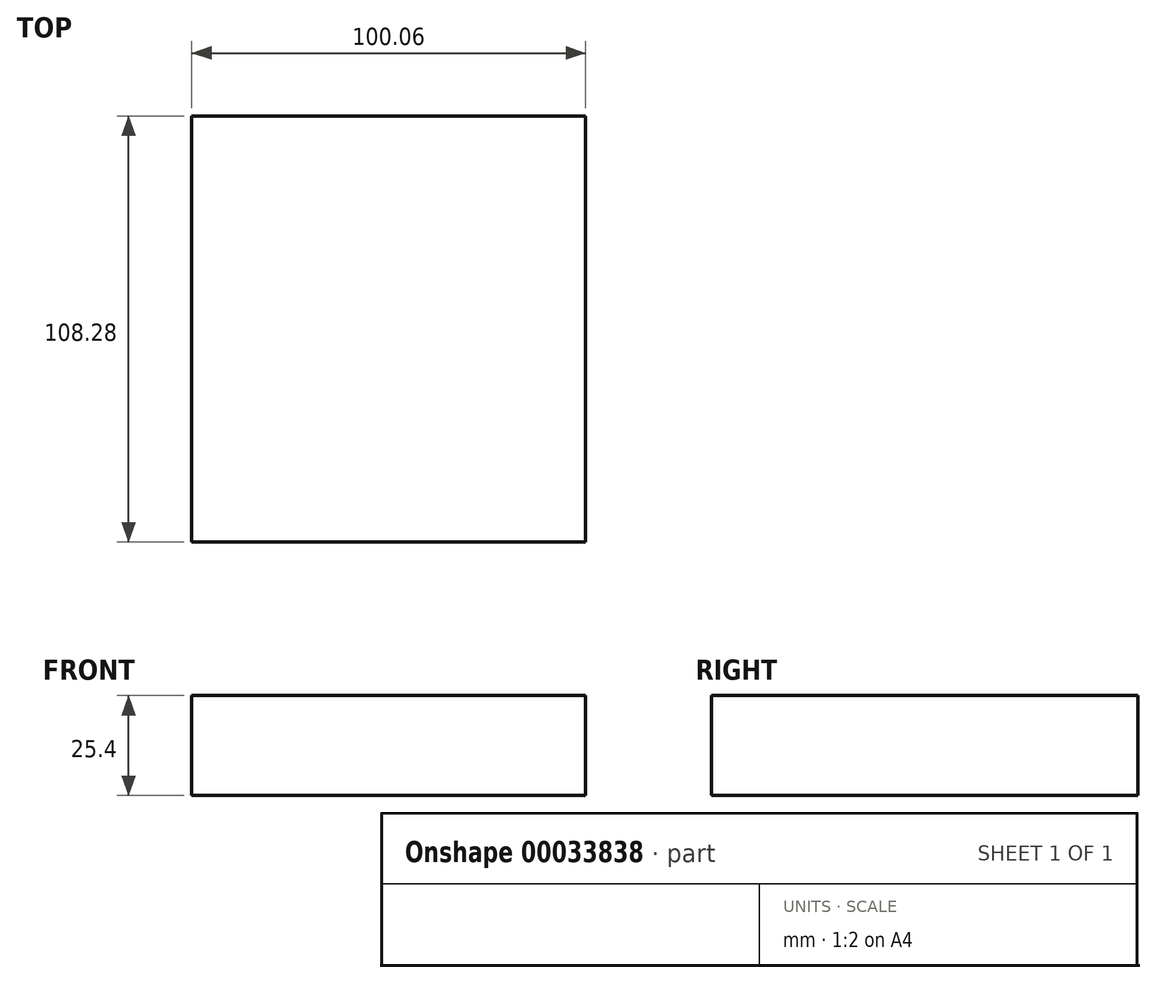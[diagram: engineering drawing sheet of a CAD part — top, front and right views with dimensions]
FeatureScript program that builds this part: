
annotation { "Feature Type Name" : "Feature", "Feature Type Description" : "" }
export const myFeature = defineFeature(function(context is Context, id is Id, definition is map)
    precondition{}
    {
        {
            var Q0;
            Q0=qCreatedBy(makeId("Top.planeOp"),FACE);
            var sketch = newSketch(context, id + "F0", { "sketchPlane" : qUnion([Q0])});
            skLineSegment(sketch, "E0", {"start": v(0, 0) * mm, "end": v(0, -170.8) * mm, "construction": true});
            skLineSegment(sketch, "E1.top", {"start": v(0, 54.14) * mm, "end": v(50.03, 54.14) * mm});
            skLineSegment(sketch, "E1.right", {"start": v(50.03, 0) * mm, "end": v(50.03, 54.14) * mm});
            skLineSegment(sketch, "E2", {"start": v(0, 0) * mm, "end": v(110.31, 0) * mm, "construction": true});
            skLineSegment(sketch, "E3.MirrorCS", {"start": v(0, -54.14) * mm, "end": v(50.03, -54.14) * mm});
            skLineSegment(sketch, "E4.MirrorCS", {"start": v(50.03, 0) * mm, "end": v(50.03, -54.14) * mm});
            skLineSegment(sketch, "E5.MirrorCS", {"start": v(0, 0) * mm, "end": v(0, 170.8) * mm});
            skLineSegment(sketch, "E6.MirrorCS", {"start": v(0, -54.14) * mm, "end": v(-50.03, -54.14) * mm});
            skLineSegment(sketch, "E7.MirrorCS", {"start": v(0, 54.14) * mm, "end": v(-50.03, 54.14) * mm});
            skLineSegment(sketch, "E8.MirrorCS", {"start": v(-50.03, 0) * mm, "end": v(-50.03, 54.14) * mm});
            skLineSegment(sketch, "E9.MirrorCS", {"start": v(-50.03, 0) * mm, "end": v(-50.03, -54.14) * mm});
            skSolve(sketch);
        }
        {
            var Q0;
            Q0 = qSketchRegion(id + "F0", true);
            extrude(context, id + "F1", {"entities" : qUnion([Q0]), "depth" : 25.4 * mm});
        }
    });
